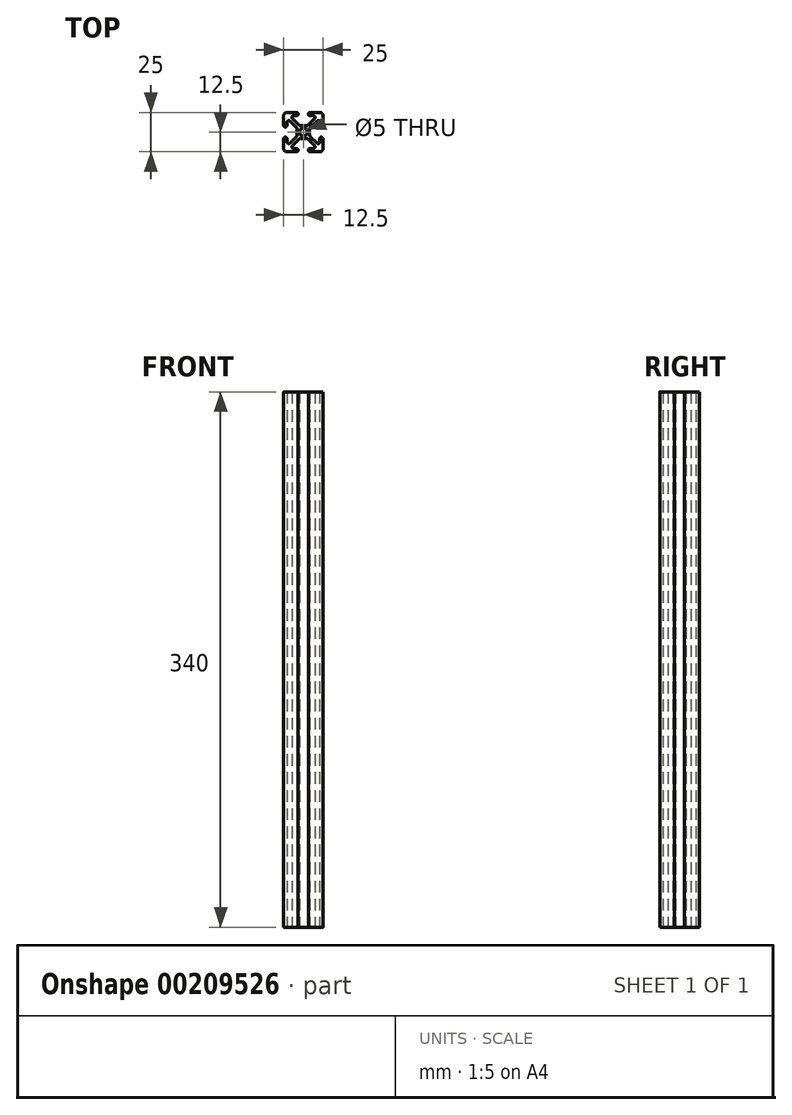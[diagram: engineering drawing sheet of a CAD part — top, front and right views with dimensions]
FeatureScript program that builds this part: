
annotation { "Feature Type Name" : "Feature", "Feature Type Description" : "" }
export const myFeature = defineFeature(function(context is Context, id is Id, definition is map)
    precondition{}
    {
        {
            var Q0;
            Q0=qCreatedBy(makeId("Top.planeOp"),FACE);
            var sketch = newSketch(context, id + "F0", { "sketchPlane" : qUnion([Q0])});
            skCircle(sketch, "E0", {"center": v(0, 0) * mm, "radius": 2.5 * mm});
            skLineSegment(sketch, "E1", {"start": v(0, 0) * mm, "end": v(0, 4.05) * mm, "construction": true});
            skLineSegment(sketch, "E2", {"start": v(0, 0) * mm, "end": v(-4.05, 0) * mm, "construction": true});
            skLineSegment(sketch, "E3", {"start": v(0, 0) * mm, "end": v(-12.5, 12.5) * mm, "construction": true});
            skLineSegment(sketch, "E4", {"start": v(-12.5, 10.36) * mm, "end": v(-12.5, 4.32) * mm});
            skLineSegment(sketch, "E5", {"start": v(-10.36, 12.5) * mm, "end": v(-4.32, 12.5) * mm});
            skLineSegment(sketch, "E6", {"start": v(-4.32, 10.36) * mm, "end": v(-6.26, 10.36) * mm});
            skLineSegment(sketch, "E7", {"start": v(-10.36, 6.26) * mm, "end": v(-10.36, 4.32) * mm});
            skArc(sketch, "E8", {"start": v(-4.32, 12.5) * mm, "mid": v(-3.25, 11.43) * mm, "end": v(-4.32, 10.36) * mm});
            skArc(sketch, "E9", {"start": v(-10.36, 4.32) * mm, "mid": v(-11.43, 3.25) * mm, "end": v(-12.5, 4.32) * mm});
            skLineSegment(sketch, "E10", {"start": v(0, 4.05) * mm, "end": v(-2.1, 4.05) * mm});
            skLineSegment(sketch, "E11", {"start": v(-4.05, 2.1) * mm, "end": v(-4.05, 0) * mm});
            skLineSegment(sketch, "E12", {"start": v(-8.53, 7.02) * mm, "end": v(-4.36, 2.85) * mm});
            skLineSegment(sketch, "E13", {"start": v(-7.02, 8.53) * mm, "end": v(-2.85, 4.36) * mm});
            skLineSegment(sketch, "E14.0.MirrorCS", {"start": v(10.36, 6.26) * mm, "end": v(10.36, 4.32) * mm});
            skLineSegment(sketch, "E14.1.MirrorCS", {"start": v(7.02, 8.53) * mm, "end": v(2.85, 4.36) * mm});
            skArc(sketch, "E14.2.MirrorCS", {"start": v(4.32, 12.5) * mm, "mid": v(3.25, 11.43) * mm, "end": v(4.32, 10.36) * mm});
            skArc(sketch, "E14.3.MirrorCS", {"start": v(10.36, 4.32) * mm, "mid": v(11.43, 3.25) * mm, "end": v(12.5, 4.32) * mm});
            skLineSegment(sketch, "E14.4.MirrorCS", {"start": v(10.36, 12.5) * mm, "end": v(4.32, 12.5) * mm});
            skLineSegment(sketch, "E14.5.MirrorCS", {"start": v(4.32, 10.36) * mm, "end": v(6.26, 10.36) * mm});
            skLineSegment(sketch, "E14.6.MirrorCS", {"start": v(12.5, 10.36) * mm, "end": v(12.5, 4.32) * mm});
            skLineSegment(sketch, "E14.7.MirrorCS", {"start": v(8.53, 7.02) * mm, "end": v(4.36, 2.85) * mm});
            skLineSegment(sketch, "E15.0.MirrorCS", {"start": v(0, 4.05) * mm, "end": v(2.1, 4.05) * mm});
            skLineSegment(sketch, "E16.0.MirrorCS", {"start": v(4.05, 2.1) * mm, "end": v(4.05, 0) * mm});
            skLineSegment(sketch, "E17.0.MirrorCS", {"start": v(10.36, -12.5) * mm, "end": v(4.32, -12.5) * mm});
            skLineSegment(sketch, "E17.1.MirrorCS", {"start": v(12.5, -10.36) * mm, "end": v(12.5, -4.32) * mm});
            skArc(sketch, "E17.2.MirrorCS", {"start": v(4.32, -12.5) * mm, "mid": v(3.25, -11.43) * mm, "end": v(4.32, -10.36) * mm});
            skLineSegment(sketch, "E17.3.MirrorCS", {"start": v(-7.02, -8.53) * mm, "end": v(-2.85, -4.36) * mm});
            skLineSegment(sketch, "E17.4.MirrorCS", {"start": v(7.02, -8.53) * mm, "end": v(2.85, -4.36) * mm});
            skLineSegment(sketch, "E17.5.MirrorCS", {"start": v(10.36, -6.26) * mm, "end": v(10.36, -4.32) * mm});
            skLineSegment(sketch, "E17.6.MirrorCS", {"start": v(8.53, -7.02) * mm, "end": v(4.36, -2.85) * mm});
            skLineSegment(sketch, "E17.7.MirrorCS", {"start": v(-10.36, -12.5) * mm, "end": v(-4.32, -12.5) * mm});
            skLineSegment(sketch, "E17.8.MirrorCS", {"start": v(-4.32, -10.36) * mm, "end": v(-6.26, -10.36) * mm});
            skLineSegment(sketch, "E17.9.MirrorCS", {"start": v(4.32, -10.36) * mm, "end": v(6.26, -10.36) * mm});
            skArc(sketch, "E17.10.MirrorCS", {"start": v(10.36, -4.32) * mm, "mid": v(11.43, -3.25) * mm, "end": v(12.5, -4.32) * mm});
            skLineSegment(sketch, "E17.11.MirrorCS", {"start": v(-12.5, -10.36) * mm, "end": v(-12.5, -4.32) * mm});
            skLineSegment(sketch, "E17.12.MirrorCS", {"start": v(0, -4.05) * mm, "end": v(2.1, -4.05) * mm});
            skArc(sketch, "E17.13.MirrorCS", {"start": v(-4.32, -12.5) * mm, "mid": v(-3.25, -11.43) * mm, "end": v(-4.32, -10.36) * mm});
            skLineSegment(sketch, "E17.14.MirrorCS", {"start": v(-8.53, -7.02) * mm, "end": v(-4.36, -2.85) * mm});
            skArc(sketch, "E17.15.MirrorCS", {"start": v(-10.36, -4.32) * mm, "mid": v(-11.43, -3.25) * mm, "end": v(-12.5, -4.32) * mm});
            skLineSegment(sketch, "E17.16.MirrorCS", {"start": v(-10.36, -6.26) * mm, "end": v(-10.36, -4.32) * mm});
            skLineSegment(sketch, "E17.17.MirrorCS", {"start": v(0, -4.05) * mm, "end": v(-2.1, -4.05) * mm});
            skLineSegment(sketch, "E18.0.MirrorCS", {"start": v(4.05, -2.1) * mm, "end": v(4.05, 0) * mm});
            skLineSegment(sketch, "E19.0.MirrorCS", {"start": v(-4.05, -2.1) * mm, "end": v(-4.05, 0) * mm});
            skPoint(sketch, "E20.visualSharp", {"position": v(-12.5, 12.5) * mm});
            skArc(sketch, "E20.filletArc", {"start": v(-10.36, 12.5) * mm, "mid": v(-11.87, 11.87) * mm, "end": v(-12.5, 10.36) * mm});
            skPoint(sketch, "E21.visualSharp", {"position": v(12.5, 12.5) * mm});
            skArc(sketch, "E21.filletArc", {"start": v(12.5, 10.36) * mm, "mid": v(11.87, 11.87) * mm, "end": v(10.36, 12.5) * mm});
            skPoint(sketch, "E22.visualSharp", {"position": v(12.5, -12.5) * mm});
            skArc(sketch, "E22.filletArc", {"start": v(10.36, -12.5) * mm, "mid": v(11.87, -11.87) * mm, "end": v(12.5, -10.36) * mm});
            skPoint(sketch, "E23.visualSharp", {"position": v(-12.5, -12.5) * mm});
            skArc(sketch, "E23.filletArc", {"start": v(-12.5, -10.36) * mm, "mid": v(-11.87, -11.87) * mm, "end": v(-10.36, -12.5) * mm});
            skPoint(sketch, "E24.visualSharp", {"position": v(4.05, 4.05) * mm});
            skPoint(sketch, "E25.visualSharp", {"position": v(-10.36, 8.85) * mm});
            skArc(sketch, "E25.filletArc", {"start": v(-8.53, 7.02) * mm, "mid": v(-9.7, 7.25) * mm, "end": v(-10.36, 6.26) * mm});
            skPoint(sketch, "E26.visualSharp", {"position": v(-8.85, 10.36) * mm});
            skArc(sketch, "E26.filletArc", {"start": v(-6.26, 10.36) * mm, "mid": v(-7.25, 9.7) * mm, "end": v(-7.02, 8.53) * mm});
            skPoint(sketch, "E27.visualSharp", {"position": v(8.85, 10.36) * mm});
            skArc(sketch, "E27.filletArc", {"start": v(7.02, 8.53) * mm, "mid": v(7.25, 9.7) * mm, "end": v(6.26, 10.36) * mm});
            skPoint(sketch, "E28.visualSharp", {"position": v(10.36, 8.85) * mm});
            skArc(sketch, "E28.filletArc", {"start": v(10.36, 6.26) * mm, "mid": v(9.7, 7.25) * mm, "end": v(8.53, 7.02) * mm});
            skPoint(sketch, "E29.visualSharp", {"position": v(10.36, -8.85) * mm});
            skArc(sketch, "E29.filletArc", {"start": v(8.53, -7.02) * mm, "mid": v(9.7, -7.25) * mm, "end": v(10.36, -6.26) * mm});
            skPoint(sketch, "E30.visualSharp", {"position": v(8.85, -10.36) * mm});
            skArc(sketch, "E30.filletArc", {"start": v(6.26, -10.36) * mm, "mid": v(7.25, -9.7) * mm, "end": v(7.02, -8.53) * mm});
            skPoint(sketch, "E31.visualSharp", {"position": v(-8.85, -10.36) * mm});
            skArc(sketch, "E31.filletArc", {"start": v(-7.02, -8.53) * mm, "mid": v(-7.25, -9.7) * mm, "end": v(-6.26, -10.36) * mm});
            skPoint(sketch, "E32.visualSharp", {"position": v(-10.36, -8.85) * mm});
            skArc(sketch, "E32.filletArc", {"start": v(-10.36, -6.26) * mm, "mid": v(-9.7, -7.25) * mm, "end": v(-8.53, -7.02) * mm});
            skPoint(sketch, "E33.orphan", {"position": v(-4.05, 4.05) * mm});
            skPoint(sketch, "E34.orphan", {"position": v(4.05, -4.05) * mm});
            skPoint(sketch, "E35.orphan", {"position": v(-4.05, -4.05) * mm});
            skPoint(sketch, "E36.visualSharp", {"position": v(-2.54, 4.05) * mm});
            skArc(sketch, "E36.filletArc", {"start": v(-2.85, 4.36) * mm, "mid": v(-2.5, 4.13) * mm, "end": v(-2.1, 4.05) * mm});
            skPoint(sketch, "E37.visualSharp", {"position": v(2.54, 4.05) * mm});
            skArc(sketch, "E37.filletArc", {"start": v(2.1, 4.05) * mm, "mid": v(2.5, 4.13) * mm, "end": v(2.85, 4.36) * mm});
            skPoint(sketch, "E38.visualSharp", {"position": v(-4.05, 2.54) * mm});
            skArc(sketch, "E38.filletArc", {"start": v(-4.05, 2.1) * mm, "mid": v(-4.13, 2.5) * mm, "end": v(-4.36, 2.85) * mm});
            skPoint(sketch, "E39.visualSharp", {"position": v(-4.05, -2.54) * mm});
            skArc(sketch, "E39.filletArc", {"start": v(-4.36, -2.85) * mm, "mid": v(-4.13, -2.5) * mm, "end": v(-4.05, -2.1) * mm});
            skPoint(sketch, "E40.visualSharp", {"position": v(-2.54, -4.05) * mm});
            skArc(sketch, "E40.filletArc", {"start": v(-2.1, -4.05) * mm, "mid": v(-2.5, -4.13) * mm, "end": v(-2.85, -4.36) * mm});
            skPoint(sketch, "E41.visualSharp", {"position": v(2.54, -4.05) * mm});
            skArc(sketch, "E41.filletArc", {"start": v(2.85, -4.36) * mm, "mid": v(2.5, -4.13) * mm, "end": v(2.1, -4.05) * mm});
            skPoint(sketch, "E42.visualSharp", {"position": v(4.05, -2.54) * mm});
            skArc(sketch, "E42.filletArc", {"start": v(4.05, -2.1) * mm, "mid": v(4.13, -2.5) * mm, "end": v(4.36, -2.85) * mm});
            skPoint(sketch, "E43.visualSharp", {"position": v(4.05, 2.54) * mm});
            skArc(sketch, "E43.filletArc", {"start": v(4.36, 2.85) * mm, "mid": v(4.13, 2.5) * mm, "end": v(4.05, 2.1) * mm});
            skSolve(sketch);
        }
        {
            var Q0;
            Q0=makeQuery(id+"F0.imprint","IMPRINT",FACE,{"disambiguationData":[TD([[makeQuery(id+"F0.imprint","IMPRINT",EDGE,{"derivedFrom":sQuery(id+"F0.wireOp",EDGE,"E0")}),-1.0]])]});
            extrude(context, id + "F1", {"entities" : qUnion([Q0]), "depth" : 340 * mm});
        }
    });
